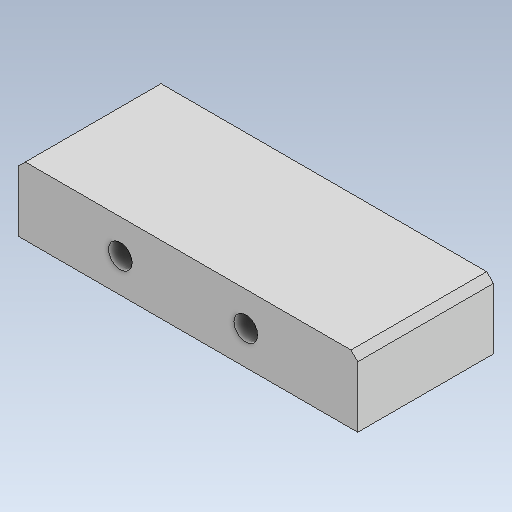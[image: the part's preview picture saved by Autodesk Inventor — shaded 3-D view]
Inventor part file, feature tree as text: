
AUTODESK INVENTOR PART (.ipt)
format: ipt  version: 2020 (Build 240168000, 168)  size: 107,520 bytes
history: native  units: mm
features: extrude x1, chamfer x1, sketch x1
ambient origin geometry x8: Origin, YZ Plane, XZ Plane, XY Plane, X Axis, Y Axis, Z Axis, Center Point
bodies: Solid1 (feature_tree)
feature tree (3):
  extrude  "Extrusion1"  Depth=100.0mm
  chamfer  "Chamfer1"  Distance=10.0mm
  sketch  "Sketch1"  dims[d0=20.0mm d1=100.0mm d2=10.0mm d3=30.0mm d4=33.0mm d5=7.0mm d6=7.0mm d7=40.0mm d8=0.0mm d9=2.0mm d10=2.0mm d11=45.0deg]
